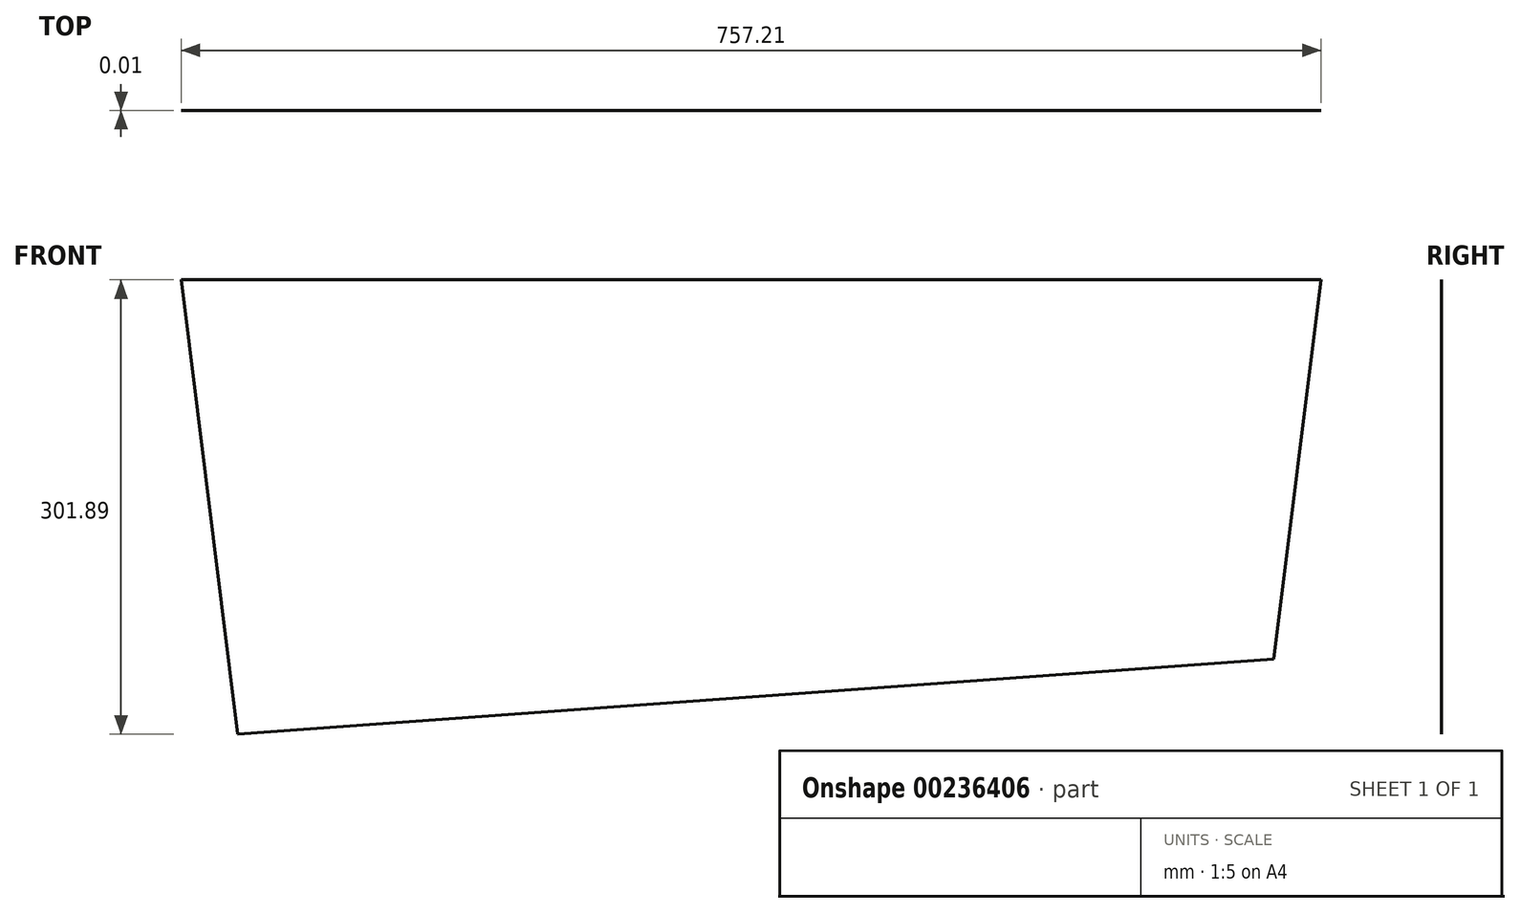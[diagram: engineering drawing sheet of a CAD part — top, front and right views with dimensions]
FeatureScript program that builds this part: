
annotation { "Feature Type Name" : "Feature", "Feature Type Description" : "" }
export const myFeature = defineFeature(function(context is Context, id is Id, definition is map)
    precondition{}
    {
        {
            var Q0;
            Q0=qCreatedBy(makeId("Front.planeOp"),FACE);
            var sketch = newSketch(context, id + "F0", { "sketchPlane" : qUnion([Q0])});
            skLineSegment(sketch, "E0", {"start": v(380.15, 138.5) * mm, "end": v(342.7, -163.4) * mm});
            skLineSegment(sketch, "E1", {"start": v(342.7, -163.4) * mm, "end": v(-345.8, -113.58) * mm});
            skLineSegment(sketch, "E2", {"start": v(-345.8, -113.58) * mm, "end": v(-377.06, 138.5) * mm});
            skLineSegment(sketch, "E3", {"start": v(-377.06, 138.5) * mm, "end": v(380.15, 138.5) * mm});
            skSolve(sketch);
        }
        {
            var Q0;
            Q0 = qSketchRegion(id + "F0", true);
            extrude(context, id + "F1", {"entities" : qUnion([Q0]), "depth" : 3 / 406.4 * mm});
        }
        {
            var Q0;
            Q0=makeQuery(id+"F1.opExtrude","SWEPT_BODY",BODY,{"disambiguationData":[OSD([sQuery(id+"F0.wireOp",EDGE,"E0"),sQuery(id+"F0.wireOp",EDGE,"E1"),sQuery(id+"F0.wireOp",EDGE,"E2"),sQuery(id+"F0.wireOp",EDGE,"E3")])]});
            var Q1;
            Q1=qCreatedBy(makeId("Right.planeOp"),FACE);
            mirror(context, id + "F2", {"entities" : qUnion([Q0]), "mirrorPlane" : qUnion([Q1])});
        }
        {
            var Q0;
            Q0=makeQuery(id+"F1.opExtrude","SWEPT_BODY",BODY,{"disambiguationData":[OSD([sQuery(id+"F0.wireOp",EDGE,"E0"),sQuery(id+"F0.wireOp",EDGE,"E1"),sQuery(id+"F0.wireOp",EDGE,"E2"),sQuery(id+"F0.wireOp",EDGE,"E3")])]});
            deleteBodies(context, id + "F3", {"entities" : qUnion([Q0])});
        }
    });
